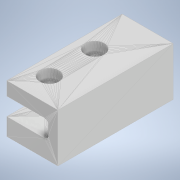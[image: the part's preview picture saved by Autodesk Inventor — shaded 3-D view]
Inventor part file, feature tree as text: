
AUTODESK INVENTOR PART (.ipt)
format: ipt  version: 2020 (Build 240168000, 168)  size: 164,864 bytes
history: native  units: mm
features: sketch x3, extrude x3, other x2, plane x1
ambient origin geometry x8: Origin, YZ Plane, XZ Plane, XY Plane, X Axis, Y Axis, Z Axis, Center Point
bodies: Volumenkörper1 (feature_tree)
feature tree (9):
  other  "GlassesInterface"
  sketch  "Skizze1"  dims[d1=0.0mm d2=10.0mm d3=0.0mm]
  sketch  "Skizze2"  dims[d4=10.0mm d5=0.0mm d6=0.5mm]
  plane  "Arbeitsebene2"
  extrude  "Extrusion1"  Depth=10.0mm TaperAngle=0.0deg
  extrude  "Extrusion2"  Depth=10.0mm
  extrude  "Extrusion3"  [1 undecoded]
  sketch  "Skizze3"  dims[d7=0.25mm d8=0.0mm]
  other  "MeshFeature1"
note: 1 required parameter value undecoded (feature->parameter linkage not recoverable at this tier; creation-order binding heuristic only, values carry confidence <= 0.55)
